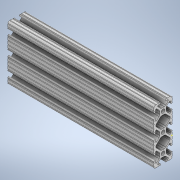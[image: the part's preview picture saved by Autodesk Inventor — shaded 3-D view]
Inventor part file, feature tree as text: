
AUTODESK INVENTOR PART (.ipt)
format: ipt  version: 2020 (Build 240168000, 168)  size: 370,688 bytes
history: native  units: in
note: dims shown in document units (in); Inventor stores cm internally (conversion verified against a paired STEP export)
features: sketch x2, extrude x1
ambient origin geometry x8: Origin, YZ Plane, XZ Plane, XY Plane, X Axis, Y Axis, Z Axis, Center Point
bodies: Solid1 (feature_tree)
feature tree (3):
  extrude  "Extrusion1"  [1 undecoded]
  sketch  "Sketch2"
  sketch  "Sketch1"  dims[d0=8.0in d1=0.0in]
note: 1 required parameter value undecoded (feature->parameter linkage not recoverable at this tier; creation-order binding heuristic only, values carry confidence <= 0.55)
